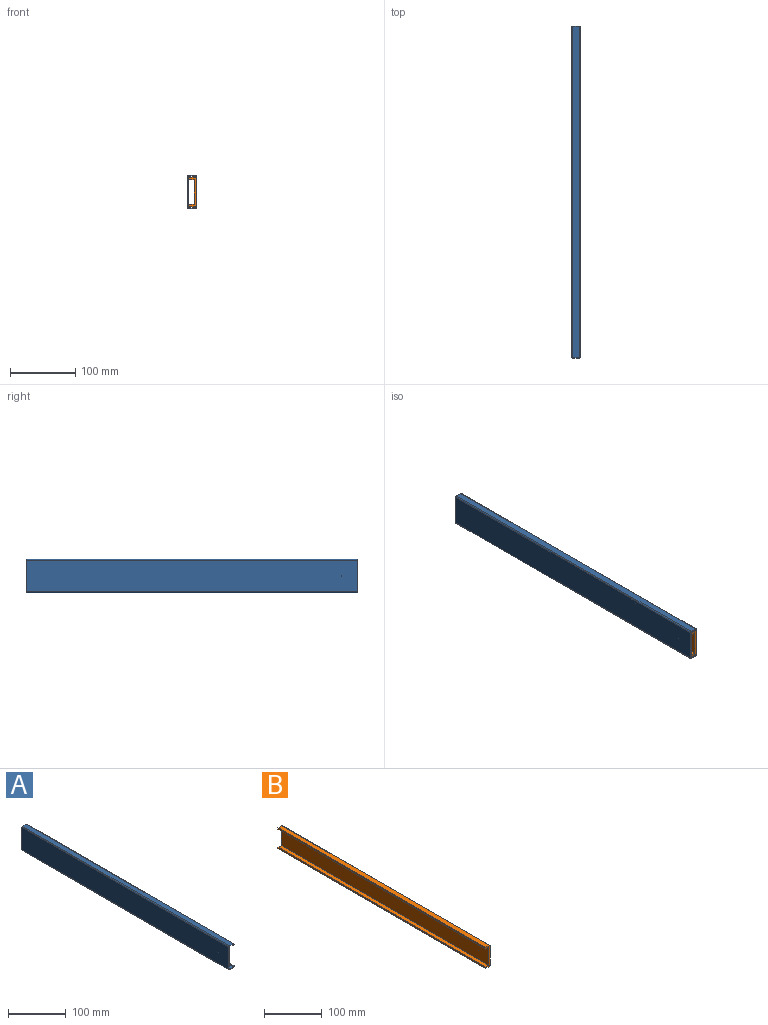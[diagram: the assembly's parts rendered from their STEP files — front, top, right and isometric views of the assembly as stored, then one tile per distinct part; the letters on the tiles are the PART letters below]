
ASSEMBLY  parts=2 mates=1
PART A: 19 faces, bbox 12.7x508x50.8 mm
  f0: plane 508x47.63mm, normal (1,0,0), area 24193.5mm2, adj f1,f15,f16,f17,f18
  f1: plane 508x9.53mm, normal (0,0,1), area 4838.7mm2, adj f0,f2,f16,f17
  f2: plane 508x1.59mm, normal (-1,0,0), area 806.4mm2, adj f1,f3,f16,f17
  f3: plane 508x1.59mm, normal (0,0,1), area 806.4mm2, adj f2,f4,f16,f17
  f4: plane 508x1.59mm, normal (1,0,0), area 806.4mm2, adj f3,f5,f16,f17
  f5: cylinder r=1.59mm len=508mm, axis (0,-1,0), area 1266.8mm2, adj f4,f6,f16,f17
  f6: plane 508x9.53mm, normal (0,0,-1), area 4838.7mm2, adj f5,f7,f16,f17
  f7: cylinder r=1.59mm len=508mm, axis (0,-1,0), area 1266.8mm2, adj f6,f8,f16,f17
  f8: plane 508x47.63mm, normal (-1,0,0), area 24193.5mm2, adj f7,f9,f16,f17,f18
  f9: cylinder r=1.59mm len=508mm, axis (0,-1,0), area 1266.8mm2, adj f8,f10,f16,f17
  f10: plane 508x9.53mm, normal (0,0,1), area 4838.7mm2, adj f9,f11,f16,f17
  f11: cylinder r=1.59mm len=508mm, axis (0,-1,0), area 1266.8mm2, adj f10,f12,f16,f17
  f12: plane 508x1.59mm, normal (1,0,0), area 806.4mm2, adj f11,f13,f16,f17
  f13: plane 508x1.59mm, normal (0,0,-1), area 806.4mm2, adj f12,f14,f16,f17
  f14: plane 508x1.59mm, normal (-1,0,0), area 806.4mm2, adj f13,f15,f16,f17
  f15: plane 508x9.53mm, normal (0,0,-1), area 4838.7mm2, adj f0,f14,f16,f17
  f16: plane 50.8x12.7mm, normal (0,1,0), area 118.8mm2, adj f0,f1,f2,f3,f4,f5,f6,f7
  f17: plane 50.8x12.7mm, normal (0,-1,0), area 118.8mm2, adj f0,f1,f2,f3,f4,f5,f6,f7
  f18: cylinder r=0.01mm len=1.59mm, axis (1,0,0), area 0.1mm2, adj f0,f8
PART B: 13 faces, bbox 11.1x508x44.5 mm
  f0: plane 508x3.18mm, normal (-1,0,0), area 1612.9mm2, adj f1,f9,f10,f11
  f1: plane 508x7.94mm, normal (0,0,1), area 4032.3mm2, adj f0,f2,f10,f11
  f2: plane 508x38.1mm, normal (-1,0,0), area 19354.8mm2, adj f1,f3,f10,f11,f12
  f3: plane 508x7.94mm, normal (0,0,-1), area 4032.3mm2, adj f2,f4,f10,f11
  f4: plane 508x3.18mm, normal (-1,0,0), area 1612.9mm2, adj f3,f5,f10,f11
  f5: plane 508x9.53mm, normal (0,0,1), area 4838.7mm2, adj f4,f6,f10,f11
  f6: cylinder r=1.59mm len=508mm, axis (0,-1,0), area 1266.8mm2, adj f5,f7,f10,f11
  f7: plane 508x41.28mm, normal (1,0,0), area 20967.7mm2, adj f6,f8,f10,f11,f12
  f8: cylinder r=1.59mm len=508mm, axis (0,-1,0), area 1266.8mm2, adj f7,f9,f10,f11
  f9: plane 508x9.53mm, normal (0,0,-1), area 4838.7mm2, adj f0,f8,f10,f11
  f10: plane 44.45x11.11mm, normal (0,1,0), area 190.5mm2, adj f0,f1,f2,f3,f4,f5,f6,f7
  f11: plane 44.45x11.11mm, normal (0,-1,0), area 190.5mm2, adj f0,f1,f2,f3,f4,f5,f6,f7
  f12: cylinder r=0.01mm len=3.18mm, axis (1,0,0), area 0.3mm2, adj f2,f7
PLACE A at identity fixed
PLACE B at identity
MATE planar A.f0 <-> B.f0  axis (1,0,0) through (1.59,-571.5,711.2)mm
